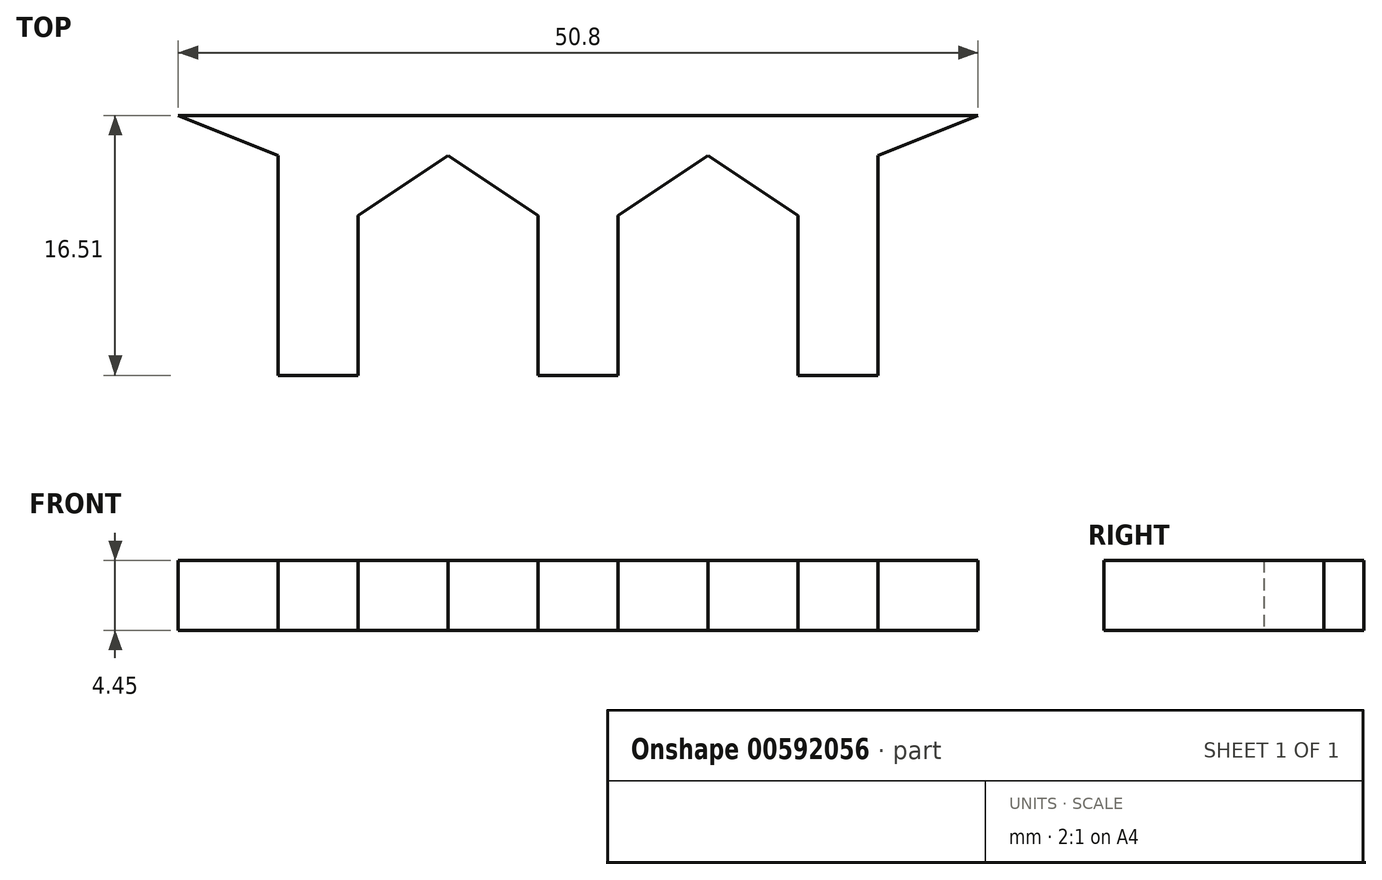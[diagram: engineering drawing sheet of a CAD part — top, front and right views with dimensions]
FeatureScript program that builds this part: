
annotation { "Feature Type Name" : "Feature", "Feature Type Description" : "" }
export const myFeature = defineFeature(function(context is Context, id is Id, definition is map)
    precondition{}
    {
        {
            var Q0;
            Q0=qCreatedBy(makeId("Top.planeOp"),FACE);
            var sketch = newSketch(context, id + "F0", { "sketchPlane" : qUnion([Q0])});
            skLineSegment(sketch, "E0.bottom", {"start": v(-13.15, 28.26) * mm, "end": v(-8.07, 28.26) * mm});
            skLineSegment(sketch, "E0.top", {"start": v(-13.15, 11.75) * mm, "end": v(-8.07, 11.75) * mm});
            skLineSegment(sketch, "E1.bottom", {"start": v(2.1, 28.26) * mm, "end": v(7.17, 28.26) * mm});
            skLineSegment(sketch, "E1.top", {"start": v(3.36, 11.75) * mm, "end": v(8.44, 11.75) * mm});
            skLineSegment(sketch, "E2.bottom", {"start": v(19.87, 28.26) * mm, "end": v(24.95, 28.26) * mm});
            skLineSegment(sketch, "E2.top", {"start": v(19.87, 11.75) * mm, "end": v(24.95, 11.75) * mm});
            skLineSegment(sketch, "E3", {"start": v(-8.07, 28.26) * mm, "end": v(19.87, 28.26) * mm});
            skLineSegment(sketch, "E4", {"start": v(-2.35, 25.72) * mm, "end": v(-8.07, 21.9) * mm});
            skLineSegment(sketch, "E5", {"start": v(-2.35, 25.72) * mm, "end": v(3.36, 21.9) * mm});
            skLineSegment(sketch, "E6", {"start": v(8.44, 21.9) * mm, "end": v(14.16, 25.72) * mm});
            skLineSegment(sketch, "E7", {"start": v(14.16, 25.72) * mm, "end": v(19.87, 21.9) * mm});
            skLineSegment(sketch, "E8", {"start": v(-13.15, 28.26) * mm, "end": v(-19.5, 28.26) * mm});
            skLineSegment(sketch, "E9", {"start": v(-19.5, 28.26) * mm, "end": v(-13.15, 25.72) * mm});
            skLineSegment(sketch, "E10", {"start": v(24.95, 28.26) * mm, "end": v(31.3, 28.26) * mm});
            skLineSegment(sketch, "E11", {"start": v(31.3, 28.26) * mm, "end": v(24.95, 25.72) * mm});
            skLineSegment(sketch, "E12", {"start": v(3.36, 21.9) * mm, "end": v(3.36, 11.75) * mm});
            skLineSegment(sketch, "E13", {"start": v(8.44, 21.9) * mm, "end": v(8.44, 11.75) * mm});
            skLineSegment(sketch, "E14", {"start": v(19.87, 21.9) * mm, "end": v(19.87, 11.75) * mm});
            skLineSegment(sketch, "E15", {"start": v(24.95, 11.75) * mm, "end": v(24.95, 25.72) * mm});
            skLineSegment(sketch, "E16", {"start": v(-13.15, 25.72) * mm, "end": v(-13.15, 11.75) * mm});
            skLineSegment(sketch, "E17", {"start": v(-8.07, 11.75) * mm, "end": v(-8.07, 21.9) * mm});
            skSolve(sketch);
        }
        {
            var Q0;
            {var subQ1=sQuery(id+"F0.wireOp",EDGE,"E0.bottom");Q0=makeQuery(id+"F0.imprint","IMPRINT",FACE,{"disambiguationData":[TD([[makeQuery(id+"F0.imprint","IMPRINT",EDGE,{"derivedFrom":subQ1}),-1.0]])]});}
            extrude(context, id + "F1", {"entities" : qUnion([Q0]), "depth" : 4.44 * mm, "offsetDistance" : 25.4 * mm});
        }
    });
